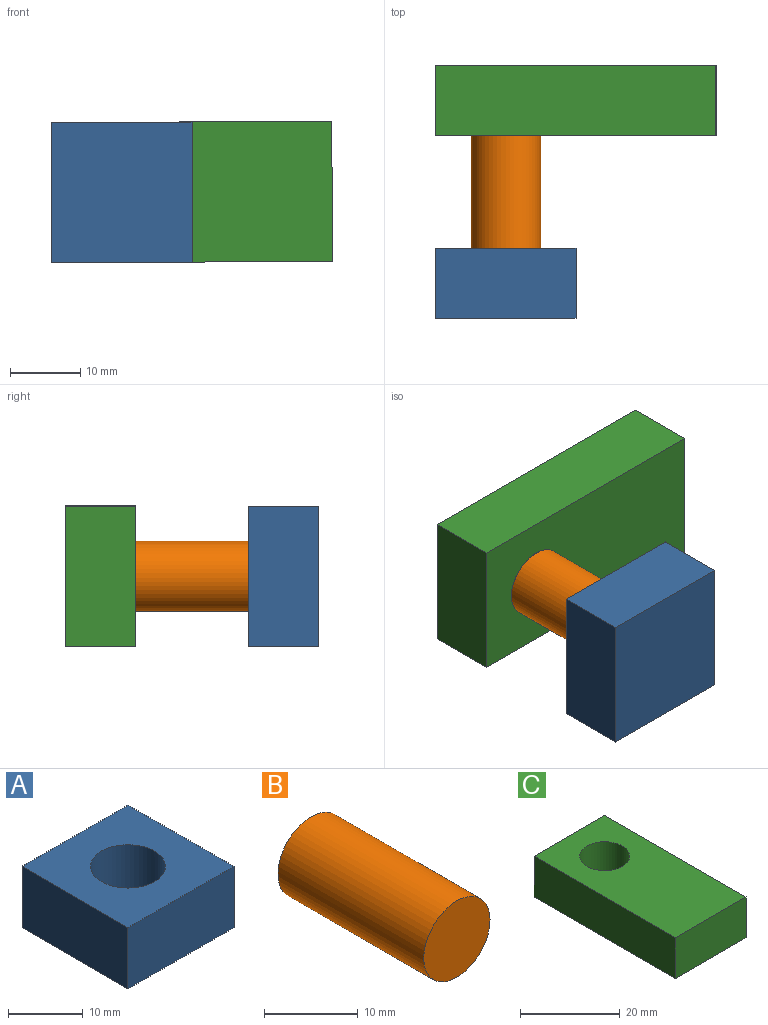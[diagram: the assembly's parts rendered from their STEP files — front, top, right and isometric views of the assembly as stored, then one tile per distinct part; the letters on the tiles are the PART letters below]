
ASSEMBLY  parts=3 mates=3
PART A: 8 faces, bbox 20x20x10 mm
  f0: plane 20x20mm, normal (0,0,1), area 321.5mm2, adj f1,f3,f4,f5,f6
  f1: plane 20x10mm, normal (-1,0,0), area 200mm2, adj f0,f2,f4,f5
  f2: plane 20x20mm, normal (0,0,-1), area 400mm2, adj f1,f3,f4,f5
  f3: plane 20x10mm, normal (1,0,0), area 200mm2, adj f0,f2,f4,f5
  f4: plane 20x10mm, normal (0,-1,0), area 200mm2, adj f0,f1,f2,f3
  f5: plane 20x10mm, normal (0,1,0), area 200mm2, adj f0,f1,f2,f3
  f6: cylinder r=5mm len=10mm, axis (0,0,1), area 251.3mm2, adj f0,f7
  f7: plane 10x10mm, normal (0,0,1), area 78.5mm2, adj f6
PART B: 3 faces, bbox 10x22x10 mm
  f0: cylinder r=5mm len=22mm, axis (0,-1,0), area 691.2mm2, adj f1,f2
  f1: plane 10x10mm, normal (0,1,0), area 78.5mm2, adj f0
  f2: plane 10x10mm, normal (0,-1,0), area 78.5mm2, adj f0
PART C: 8 faces, bbox 20x40x10 mm
  f0: plane 40x20mm, normal (0,0,1), area 721.5mm2, adj f1,f3,f4,f5,f6
  f1: plane 40x10mm, normal (-1,0,0), area 400mm2, adj f0,f2,f4,f5
  f2: plane 40x20mm, normal (0,0,-1), area 800mm2, adj f1,f3,f4,f5
  f3: plane 40x10mm, normal (1,0,0), area 400mm2, adj f0,f2,f4,f5
  f4: plane 20x10mm, normal (0,-1,0), area 200mm2, adj f0,f1,f2,f3
  f5: plane 20x10mm, normal (0,1,0), area 200mm2, adj f0,f1,f2,f3
  f6: cylinder r=5mm len=10mm, axis (0,0,1), area 251.3mm2, adj f0,f7
  f7: plane 10x10mm, normal (0,0,1), area 78.5mm2, adj f6
PLACE A rot(axis=(0,0.71,0.71),180deg) t=(10,0,20)mm
PLACE B rot(axis=(0,1,0),43.3deg) t=(10,15.1,10)mm
PLACE C rot(axis=(0.58,-0.58,0.58),120deg) t=(10,36.1,10)mm
MATE planar A.f6 <-> B.f0  axis (0,1,0) through (10,2,10)mm
MATE cylindrical B.f0 <-> A.f6  axis (0,-1,0) through (10,15.1,10)mm
MATE revolute C.f6 <-> B.f0  axis (0,-1,0) through (10,26.1,10)mm
